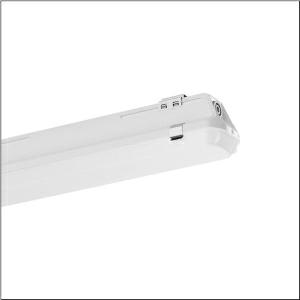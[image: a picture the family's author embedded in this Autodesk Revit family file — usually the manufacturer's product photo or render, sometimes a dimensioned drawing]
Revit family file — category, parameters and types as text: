
# Revit family: monsun_r__21_51fb10dp430b_6f0c
name_source: partatom
category: Lighting Fixtures
units: mm (PartAtom-declared; Revit-internal decimal feet)

## family parameters
Cut with Voids When Loaded = No
Host = Face
Light Source = No
Part Type = Normal
Room Calculation Point = No
Round Connector Dimension = Use Diameter
Shared = No

## types (1)
- --- (1 x LED, 3860 lm, 24.7 W, 4000K)
    Apparent Load = 25 VA
    CIE Flux Codes = 47 77 93 94 100
    Color Rendering = 80
    Color Temperature = 4000K
    Default Elevation = 1800 mm
    Description = Monsun® 21, damp-proof luminaire, chain hanger, primary optical cover: enclosure, of PMMA, light emission: direct distribution, primary light characteristic: symmetric, installation type: suspended mounting, surface-mounted, horizontal mounting, vertical mounting, LED, rated luminous flux: 3.860lm, luminous efficacy: 156lm/W, light colour: 840, colour temperature: 4000K, control gear: ECG DALI, with terminal, 5-pole, max. 2.5mm², mains connection: 220..240V, AC, 50/60Hz, rated input power: 25W, housing, of glass-fibre reinforced polyester, uncoated, bright grey, incl. chain hanger, length: 1.590mm, width: 90mm, height: 88mm, clip for enclosure, of stainless steel (V2A), ceiling mounting element, of stainless steel (V2A), chain hanger, of stainless steel (V2A), protection rating (complete): IP66, insulation class (complete): insulation class I (protective earthing), certification: CE, ENEC, VDE, UKCA, protection symbol: D, impact resistance: IK04, permissible operating ambient temperature: -25..+35°C, standard: EN 50419, EN 60598-2-1, corresponds to IFS (International Featured Standards) requirements for safety and quality in the food industry, for indoor or canopied outdoor use, no direct snow, no direct sun, no direct rain, contact your sales advisor before using the luminaires in applications with unclear chemical exposure, large temperature fluctuations or condensation-forming humidity, LABS conformity tested according to VDMA 24364:2018-05, packaging unit: 1 piece
    Height = 89 mm
    Lamp = 1 x LED
    Lamp Light Flux = 3860 lm
    Lamp Power = 24.7 W
    Lamp count = 1
    Length = 1590 mm
    Luminous efficacy = 156 lm/W
    Manufacturer = Siteco
    ModVariant = No
    Model = 51FB10DP430B
    Mounting Place = Ceiling
    Mounting Type = Surface mounted
    Number of Poles = 1
    OnlyDefault = Yes
    Power Factor = 1
    Product Name = Monsun® 21
    Product group = damp-proof luminaire
    ProductGroupID = 301
    Protection Class = Protection class I
    Protection Degree = IP 66
    RLX_Detail_Level = 1
    RLX_Emergency_Light_Flux = 0 lm
    RLX_Emergency_Type = 0
    RLX_Emergency_Type_DB = No
    RlxData = <blob elided: 92177 chars, md5=18cd4977>
    Socket = socket
    Standby Power = 0 W
    System Light Flux = 3860 lm
    System Power = 25 W
    Type Comments = factory setting: luminous flux: 100 % | dim-lin: 254 | 162 mA
    Type Image = l_1006717.jpg
    URL = http://relux.com
    VarID = @adj_152415
    Voltage = 0 V
    Weight = 0.00 kg
    Width = 90 mm

## geometry (parser evidence)
native form markers: Blend x4, Sweep x13
no freeform markers — native parametric forms only
